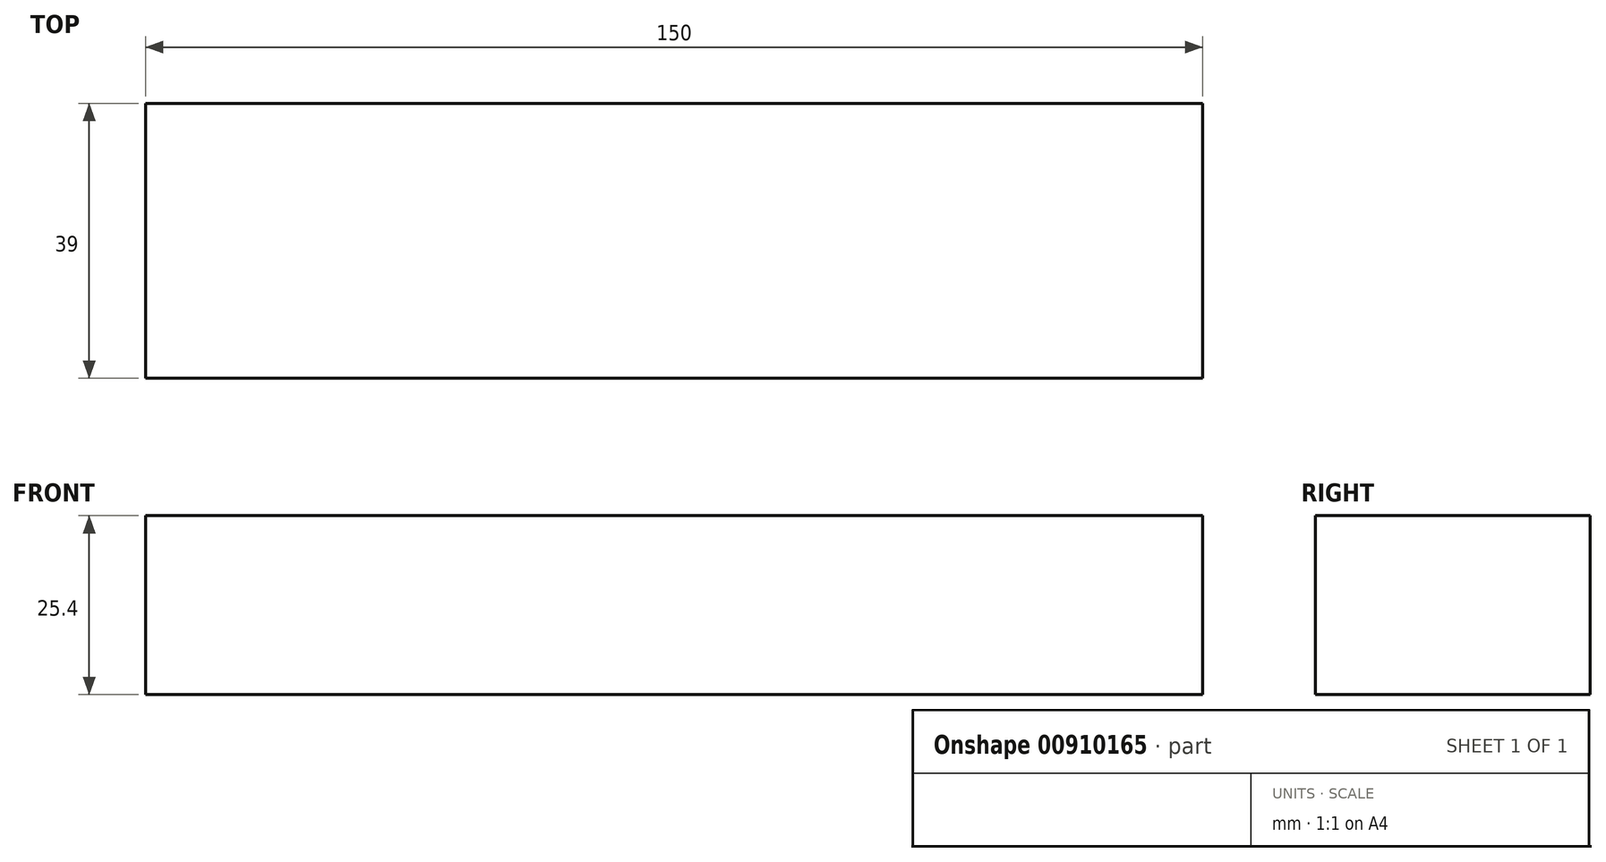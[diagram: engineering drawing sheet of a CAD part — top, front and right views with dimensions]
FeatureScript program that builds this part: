
annotation { "Feature Type Name" : "Feature", "Feature Type Description" : "" }
export const myFeature = defineFeature(function(context is Context, id is Id, definition is map)
    precondition{}
    {
        {
            var Q0;
            Q0=qCreatedBy(makeId("Top.planeOp"),FACE);
            var sketch = newSketch(context, id + "F0", { "sketchPlane" : qUnion([Q0])});
            skLineSegment(sketch, "E0.bottom", {"start": v(-150, 39) * mm, "end": v(0, 39) * mm});
            skLineSegment(sketch, "E0.top", {"start": v(-150, 0) * mm, "end": v(0, 0) * mm});
            skLineSegment(sketch, "E0.left", {"start": v(-150, 39) * mm, "end": v(-150, 0) * mm});
            skLineSegment(sketch, "E0.right", {"start": v(0, 39) * mm, "end": v(0, 0) * mm});
            skSolve(sketch);
        }
        {
            var Q0;
            Q0 = qSketchRegion(id + "F0", true);
            extrude(context, id + "F1", {"entities" : qUnion([Q0]), "depth" : 25.4 * mm, "offsetDistance" : 25 * mm});
        }
    });
